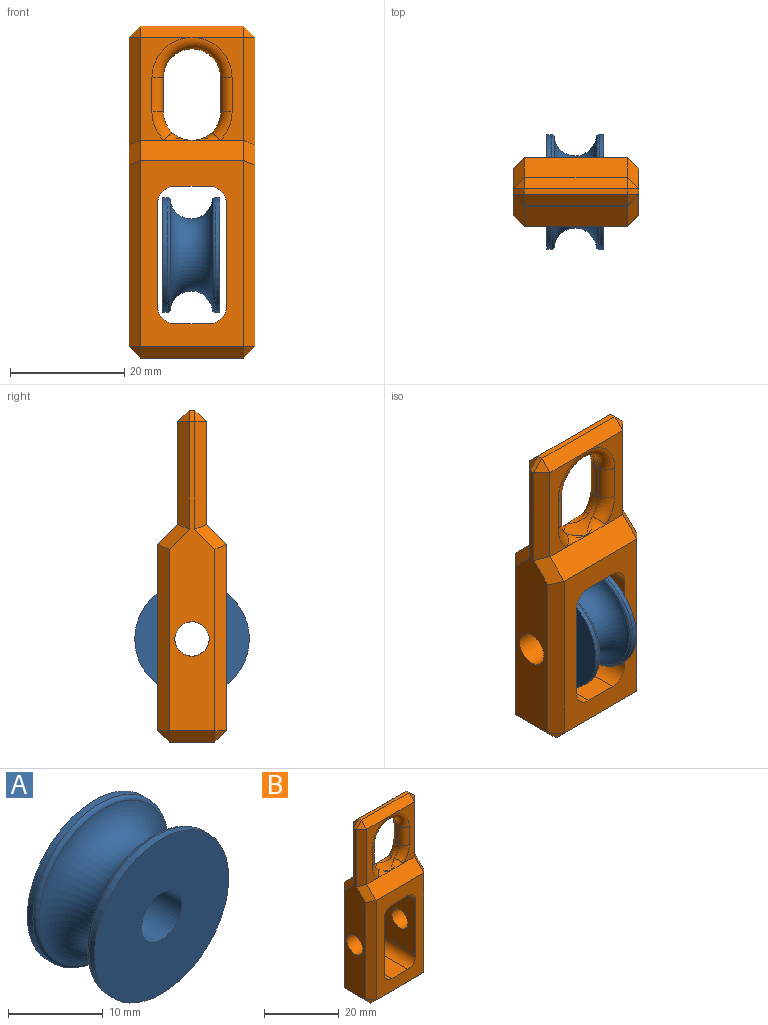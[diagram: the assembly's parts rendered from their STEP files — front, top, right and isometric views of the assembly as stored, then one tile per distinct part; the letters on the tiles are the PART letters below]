
ASSEMBLY  parts=2 mates=1
PART A: 8 faces, bbox 21.6x10x21.6 mm
  f0: plane 20x20mm, normal (0,-1,0), area 285.9mm2, adj f1,f7
  f1: cylinder r=3mm len=10mm, axis (0,-1,0), area 188.5mm2, adj f0,f2
  f2: plane 20x20mm, normal (0,1,0), area 285.9mm2, adj f1,f3
  f3: cylinder r=10mm len=20mm, axis (0,-1,0), area 52.1mm2, adj f2,f4
  f4: torus R=9.5mm, axis (0,-1,0), area 44.9mm2, adj f3,f5
  f5: torus R=10mm, axis (0,-1,0), area 504.1mm2, adj f4,f6
  f6: torus R=9.5mm, axis (0,-1,0), area 44.9mm2, adj f5,f7
  f7: cylinder r=10mm len=20mm, axis (0,-1,0), area 52.1mm2, adj f0,f6
PART B: 68 faces, bbox 22x12x58.1 mm
  f0: plane 18x9mm, normal (0,1,0), area 49.8mm2, adj f19,f41,f49,f63,f65,f67
  f1: plane 18x9mm, normal (0,-1,0), area 49.8mm2, adj f20,f39,f48,f56,f58,f60
  f2: plane 54x8mm, normal (1,0,0), area 259.7mm2, adj f17,f33,f38,f42,f43,f46,f47,f50
  f3: plane 32.5x18mm, normal (0,-1,0), area 304.7mm2, adj f8,f9,f10,f11,f12,f13,f14,f15
  f4: plane 18x1mm, normal (0,0,1), area 18mm2, adj f40,f48,f49,f53
  f5: plane 54x8mm, normal (-1,0,0), area 259.7mm2, adj f16,f26,f30,f31,f35,f36,f39,f40
  f6: plane 32.5x18mm, normal (0,1,0), area 304.7mm2, adj f8,f9,f10,f11,f12,f13,f14,f15
  f7: plane 18x8mm, normal (0,0,-1), area 144mm2, adj f26,f29,f32,f33
  f8: plane 18x12mm, normal (-1,0,0), area 187.7mm2, adj f3,f6,f9,f15,f17
  f9: cylinder r=3mm len=12mm, axis (0,-1,0), area 56.5mm2, adj f3,f6,f8,f10
  f10: plane 12x6mm, normal (0,0,-1), area 72mm2, adj f3,f6,f9,f11
  f11: cylinder r=3mm len=12mm, axis (0,-1,0), area 56.5mm2, adj f3,f6,f10,f12
  f12: plane 18x12mm, normal (1,0,0), area 187.7mm2, adj f3,f6,f11,f13,f16
  f13: cylinder r=3mm len=12mm, axis (0,-1,0), area 56.5mm2, adj f3,f6,f12,f14
  f14: plane 12x6mm, normal (0,0,1), area 72mm2, adj f3,f6,f13,f15
  f15: cylinder r=3mm len=12mm, axis (0,-1,0), area 56.5mm2, adj f3,f6,f8,f14
  f16: cylinder r=3mm len=6mm, axis (1,0,0), area 94.2mm2, adj f5,f12
  f17: cylinder r=3mm len=6mm, axis (1,0,0), area 94.2mm2, adj f2,f8
  f18: plane 18x9mm, normal (0,1,0), area 49.8mm2, adj f19,f49,f50,f64,f66,f67
  f19: plane 18x3.5mm, normal (0,0.71,0.71), area 89.1mm2, adj f0,f6,f18,f36,f46,f61,f62
  f20: plane 18x3.5mm, normal (0,-0.71,0.71), area 89.1mm2, adj f1,f3,f21,f35,f43,f54,f55
  f21: plane 18x9mm, normal (0,-1,0), area 49.8mm2, adj f20,f47,f48,f57,f59,f60
  f22: cylinder r=5mm len=10mm, axis (0,-1,0), area 27.6mm2, adj f23,f25,f54,f55,f56,f57,f61,f62
  f23: plane 6x1mm, normal (1,0,0), area 6mm2, adj f22,f24,f58,f65
  f24: cylinder r=5mm len=10mm, axis (0,-1,0), area 15.7mm2, adj f23,f25,f60,f67
  f25: plane 6x1mm, normal (-1,0,0), area 6mm2, adj f22,f24,f59,f66
  f26: plane 8x2mm, normal (-0.71,0,-0.71), area 22.6mm2, adj f5,f7,f27,f28
  f27: plane 2x2mm, normal (-0.58,-0.58,-0.58), area 3.5mm2, adj f26,f29,f30
  f28: plane 2x2mm, normal (-0.58,0.58,-0.58), area 3.5mm2, adj f26,f31,f32
  f29: plane 18x2mm, normal (0,-0.71,-0.71), area 50.9mm2, adj f3,f7,f27,f34
  f30: plane 32.5x2mm, normal (-0.71,-0.71,0), area 90.8mm2, adj f3,f5,f27,f35
  f31: plane 32.5x2mm, normal (-0.71,0.71,0), area 90.8mm2, adj f5,f6,f28,f36
  f32: plane 18x2mm, normal (0,0.71,-0.71), area 50.9mm2, adj f6,f7,f28,f37
  f33: plane 8x2mm, normal (0.71,0,-0.71), area 22.6mm2, adj f2,f7,f34,f37
  f34: plane 2x2mm, normal (0.58,-0.58,-0.58), area 3.5mm2, adj f29,f33,f38
  f35: plane 5.5x4.33mm, normal (-0.71,-0.5,0.5), area 14mm2, adj f5,f20,f30,f39
  f36: plane 5.5x4.33mm, normal (-0.71,0.5,0.5), area 14mm2, adj f5,f19,f31,f41
  f37: plane 2x2mm, normal (0.58,0.58,-0.58), area 3.5mm2, adj f32,f33,f42
  f38: plane 32.5x2mm, normal (0.71,-0.71,0), area 90.8mm2, adj f2,f3,f34,f43
  f39: plane 18.83x2mm, normal (-0.71,-0.71,0), area 52.1mm2, adj f1,f5,f35,f44
  f40: plane 2x2mm, normal (-0.71,0,0.71), area 2.8mm2, adj f4,f5,f44,f45
  f41: plane 18.83x2mm, normal (-0.71,0.71,0), area 52.1mm2, adj f0,f5,f36,f45
  f42: plane 32.5x2mm, normal (0.71,0.71,0), area 90.8mm2, adj f2,f6,f37,f46
  f43: plane 5.5x4.33mm, normal (0.71,-0.5,0.5), area 14mm2, adj f2,f20,f38,f47
  f44: plane 2x2mm, normal (-0.58,-0.58,0.58), area 3.5mm2, adj f39,f40,f48
  f45: plane 2x2mm, normal (-0.58,0.58,0.58), area 3.5mm2, adj f40,f41,f49
  f46: plane 5.5x4.33mm, normal (0.71,0.5,0.5), area 14mm2, adj f2,f19,f42,f50
  f47: plane 18.83x2mm, normal (0.71,-0.71,0), area 52.1mm2, adj f2,f21,f43,f51
  f48: plane 18x2mm, normal (0,-0.71,0.71), area 50.9mm2, adj f1,f4,f21,f44,f51
  f49: plane 18x2mm, normal (0,0.71,0.71), area 50.9mm2, adj f0,f4,f18,f45,f52
  f50: plane 18.83x2mm, normal (0.71,0.71,0), area 52.1mm2, adj f2,f18,f46,f52
  f51: plane 2x2mm, normal (0.58,-0.58,0.58), area 3.5mm2, adj f47,f48,f53
  f52: plane 2x2mm, normal (0.58,0.58,0.58), area 3.5mm2, adj f49,f50,f53
  f53: plane 2x2mm, normal (0.71,0,0.71), area 2.8mm2, adj f2,f4,f51,f52
  f54: bspline ~5.05x2.1mm, area 6.1mm2, adj f20,f22,f56
  f55: bspline ~4.9x2mm, area 6.1mm2, adj f20,f22,f57
  f56: torus R=7mm, axis (0,-1,0), area 14.3mm2, adj f1,f22,f54,f58
  f57: torus R=7mm, axis (0,-1,0), area 14.3mm2, adj f21,f22,f55,f59
  f58: cylinder r=2mm len=6mm, axis (0,0,-1), area 18.8mm2, adj f1,f23,f56,f60
  f59: cylinder r=2mm len=6mm, axis (0,0,1), area 18.8mm2, adj f21,f25,f57,f60
  f60: torus R=7mm, axis (0,-1,0), area 56.5mm2, adj f1,f21,f24,f58,f59
  f61: bspline ~5.05x2.1mm, area 6.1mm2, adj f19,f22,f63
  f62: bspline ~4.9x2mm, area 6.1mm2, adj f19,f22,f64
  f63: torus R=7mm, axis (0,-1,0), area 14.3mm2, adj f0,f22,f61,f65
  f64: torus R=7mm, axis (0,-1,0), area 14.3mm2, adj f18,f22,f62,f66
  f65: cylinder r=2mm len=6mm, axis (0,0,1), area 18.8mm2, adj f0,f23,f63,f67
  f66: cylinder r=2mm len=6mm, axis (0,0,-1), area 18.8mm2, adj f18,f25,f64,f67
  f67: torus R=7mm, axis (0,-1,0), area 56.5mm2, adj f0,f18,f24,f65,f66
PLACE A rot(axis=(-0.54,0.54,0.64),114.4deg) t=(-0.25,0.1,-8.21)mm
PLACE B t=(-0.11,6.1,2.79)mm fixed
MATE cylindrical A.f1 <-> B.f16  axis (1,0,0) through (4.75,0.1,-8.21)mm
